# Revit family: ShowerHead-HandshowerSet-220-Vitra-AquaHeatSeries-A47200
name_source: partatom
category: Plumbing Fixtures
revit_build: Autodesk Revit 2017 (Build: 20160225_1515(x64)
units: mm (PartAtom-declared; Revit-internal decimal feet)

## family parameters
Cut with Voids When Loaded = No
Host = Face
OmniClass Number = 23.45.55.17
OmniClass Title = Mixing Faucets
Part Type = Normal
Room Calculation Point = No
Round Connector Dimension = Use Diameter
Shared = Yes

## types (1)
- ShowerHead-HandshowerSet-220-Vitra-AquaHeatSeries-A47200
    Article No. (default) = A47200
    BIMobject category = Bath/Shower Mixer
    Brand = VitrA
    CW Connection = Yes
    Color = Chrome
    Connection Diameter (mm) = 20 mm  [stored 0.0656168 ft]
    Default Elevation = 850 mm  [stored 2.78871 ft]
    Description = AquaHeat 220
    Design country = Turkey
    HW Connection = Yes
    Hot Water Supply (max.) = 80 °C
    Hot Water temperature, factory set to = 38 °C
    IFC Classification = Sanitary Terminal
    Main Material = Brass
    Manufacturer = Vitra
    Manufacturer name = Vitra
    Masterformat 2014 Code = 22 41 23
    Masterformat 2014 Description = Residential Showers
    Min. flow pressure of = 0.5 bar
    Model = A47200
    Mounting type = Wall Mounted
    NBS Referans Code = 35-06-81
    NBS Referans Description = Shower Heads
    Nominal Depth (mm) = 550 mm
    Nominal Height (mm) = 1600 mm  [stored 5.24934 ft]
    Nominal Width (mm) = 270 mm  [stored 0.885827 ft]
    Number Of Connections = 2
    OmniClass Code = 23-31 17 19
    OmniClass Description = Shower Head Fixtures
    Primary Material = Chrome
    Product Properties = AquaHeat 220
    Product SKU = A47200
    Product Type = Showerhead
    Product certification = https://www.vitraglobal.com
    Product family = Shower System
    Product group = HandshowerSet
    Product url = https://www.vitra.com.tr
    Range of Hot Water Supply = 5 - 65 °C
    Range of flow pressure = 0.5-10 bar (Recommended 3-5 Bars)
    Technical description = https://www.vitra.com.tr
    Test Pressure = 16 bar
    URL = https://vitraglobal.com
    Uniclass 1.4 Code = L7214
    Uniclass 1.4 Description = Showers
    Uniclass 2.0 Code = PR-35-06-81
    Uniclass 2.0 Description = Shower Heads
    Uniclass 2015 Code = Pr_40_20_87_76
    Uniclass 2015 Name = Shower heads
    Uniformat II Code = D2010
    Uniformat II Description = Plumbing Fixtures
    Vent Connection = No
    Warranty Period (Year) = 5 Years
    Waste Connection = No
    Weight Net (kg) = 3.4
    Youtube = https://www.youtube.com

note: [stored X ft] marks values corroborated as IEEE doubles in the binary element streams (Revit-internal decimal feet)

## geometry (parser evidence)
native form markers: Sweep x2
no freeform markers — native parametric forms only
